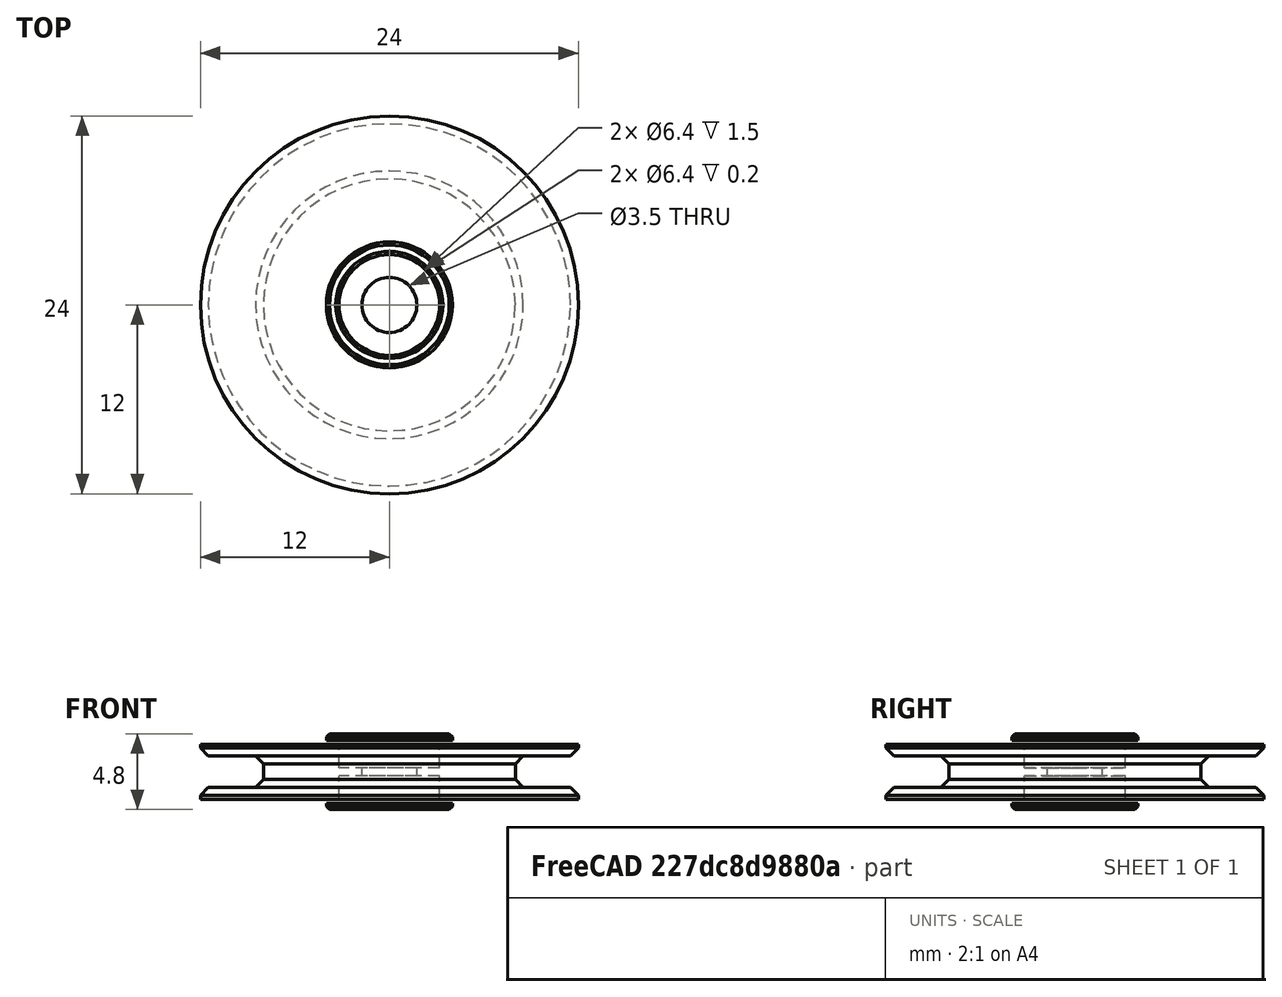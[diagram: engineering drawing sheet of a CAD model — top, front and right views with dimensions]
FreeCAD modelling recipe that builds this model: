
FCSTD DOCUMENT  (FreeCAD 0.15R4671 (Git))
Label: big_pulley_w_bearing
License: All rights reserved
LicenseURL: http://en.wikipedia.org/wiki/All_rights_reserved
objects: Part::Cylinder×8, Part::MultiFuse×2, Part::Chamfer×2, Part::Cut×1
note: 13 computed .brp shape members not serialized (recipe doc carries the construction recipe); baked Part::Feature solids carry a one-line shape summary decoded from their .brp

FEATURE [Part::Cylinder] Cylinder
  Angle = 360
  Height = 3.5
  Placement = pos=(0,0,0.25) rot=(0,0,1;0rad)
  Radius = 8
FEATURE [Part::Cylinder] Cylinder001
  Angle = 360
  Height = 0.75
  Placement = pos=(0,0,0.25) rot=(0,0,1;0rad)
  Radius = 12
FEATURE [Part::Cylinder] Cylinder003
  Angle = 360
  Height = 2.25
  Placement = pos=(0,0,2.25) rot=(0,0,1;0rad)
  Radius = 3.2
FEATURE [Part::Cylinder] Cylinder004
  Angle = 360
  Height = 10
  Placement = pos=(0,0,-1) rot=(0,0,1;0rad)
  Radius = 1.75
FEATURE [Part::Cylinder] Cylinder005
  Angle = 360
  Height = 0.4
  Placement = pos=(0,0,-0.4) rot=(0,0,1;0rad)
  Radius = 4
FEATURE [Part::Cylinder] Cylinder006
  Angle = 360
  Height = 0.75
  Placement = pos=(0,0,3) rot=(0,0,1;0rad)
  Radius = 12
FEATURE [Part::Cylinder] Cylinder007
  Angle = 360
  Height = 0.4
  Placement = pos=(0,0,4) rot=(0,0,1;0rad)
  Radius = 4
FEATURE [Part::MultiFuse] Fusion
  Shapes = -> [Cylinder,Cylinder001,Cylinder007,Cylinder006,Cylinder005]
FEATURE [Part::Cylinder] Cylinder008
  Angle = 360
  Height = 2.25
  Placement = pos=(0,0,-0.5) rot=(0,0,1;0rad)
  Radius = 3.2
FEATURE [Part::MultiFuse] Fusion001
  Shapes = -> [Cylinder008,Cylinder004,Cylinder003]
FEATURE [Part::Cut] Cut
  Base = -> Fusion
  Tool = -> Fusion001
FEATURE [Part::Chamfer] Chamfer
  Base = -> Cut
  Edges = 4 edges r=0.2: [Edge3,Edge5,Edge27,Edge30]
FEATURE [Part::Chamfer] Chamfer001
  Base = -> Chamfer
  Edges = 4 edges r=0.5: [Edge23,Edge25,Edge27,Edge31]
